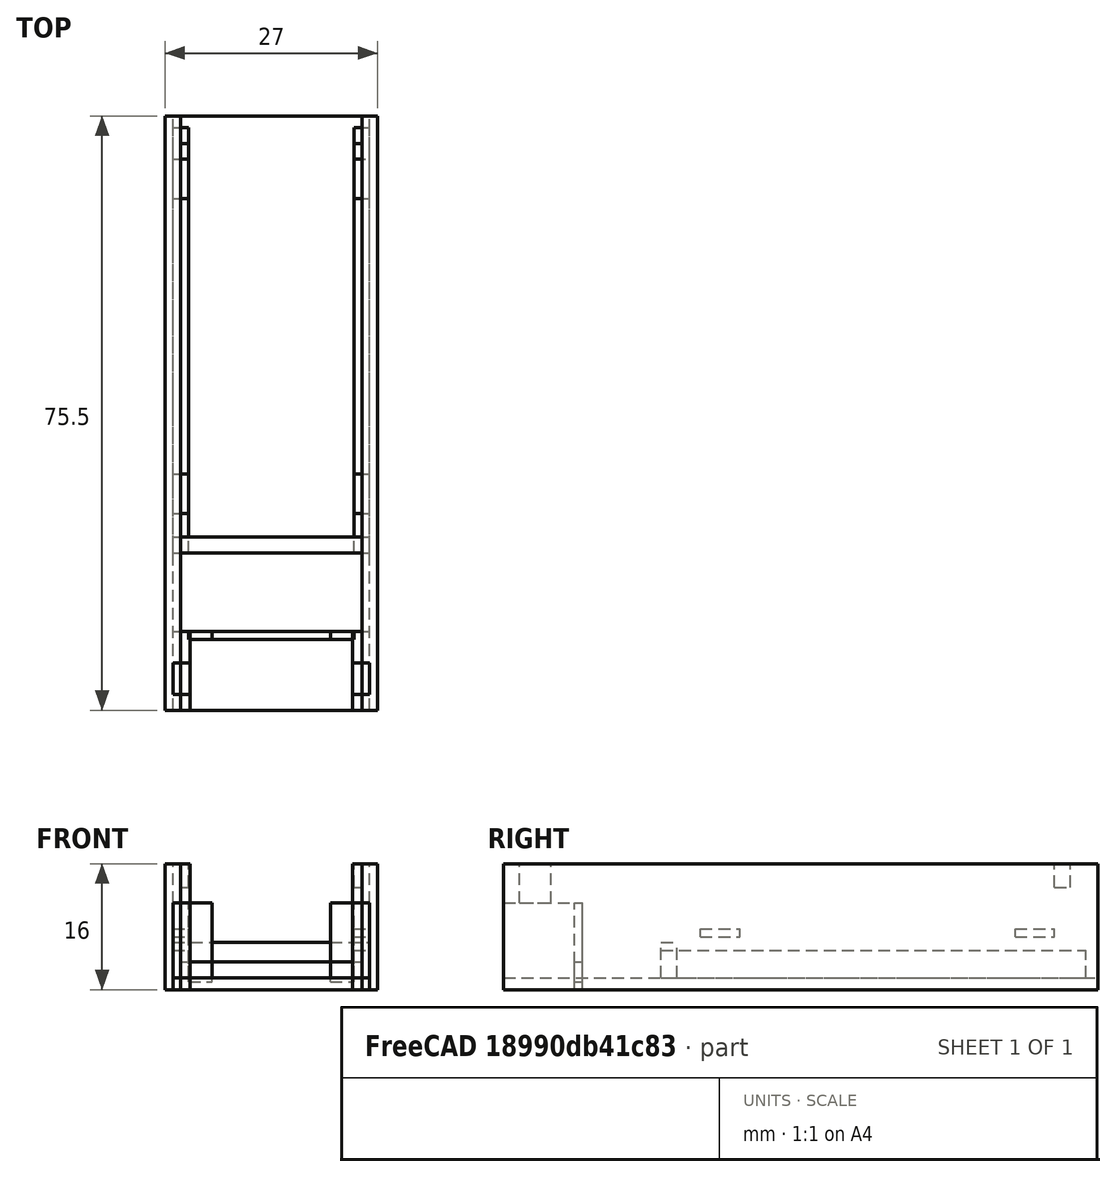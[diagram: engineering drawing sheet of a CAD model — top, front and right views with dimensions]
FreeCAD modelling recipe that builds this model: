
FCSTD DOCUMENT  (FreeCAD 0.20R29177 (Git))
Label: Anlogic FPGA programer
License: All rights reserved
LicenseURL: http://en.wikipedia.org/wiki/All_rights_reserved
objects: Part::Box×19
note: 19 computed .brp shape members not serialized (recipe doc carries the construction recipe); baked Part::Feature solids carry a one-line shape summary decoded from their .brp

FEATURE [Part::Box] Box  label="Kocka"
  AttacherType = Attacher::AttachEngine3D
  Height = 1.5
  Length = 25
  Placement = pos=(0,-20,0) rot=(0,0,1;0rad)
  Width = 75.5
FEATURE [Part::Box] Box001  label="Kocka001"
  AttacherType = Attacher::AttachEngine3D
  Height = 3.5
  Length = 2
  Placement = pos=(0,0,1.5) rot=(0,0,1;0rad)
  Width = 54
FEATURE [Part::Box] Box002  label="Kocka002"
  AttacherType = Attacher::AttachEngine3D
  Height = 16
  Length = 2
  Placement = pos=(-1,-20,0) rot=(0,0,1;0rad)
  Width = 75.5
FEATURE [Part::Box] Box005  label="Kocka005"
  AttacherType = Attacher::AttachEngine3D
  Height = 3.5
  Length = 2
  Placement = pos=(23,0,1.5) rot=(0,0,1;0rad)
  Width = 54
FEATURE [Part::Box] Box006  label="Kocka006"
  AttacherType = Attacher::AttachEngine3D
  Height = 16
  Length = 2
  Placement = pos=(24,-20,0) rot=(0,0,1;0rad)
  Width = 75.5
FEATURE [Part::Box] Box007  label="Kocka007"
  AttacherType = Attacher::AttachEngine3D
  Height = 4.5
  Length = 25
  Placement = pos=(0,0,1.5) rot=(0,0,1;0rad)
  Width = 2
FEATURE [Part::Box] Box008  label="Kocka008"
  AttacherType = Attacher::AttachEngine3D
  Height = 1
  Length = 2
  Placement = pos=(0,5,6.7) rot=(0,0,1;0rad)
  Width = 5
FEATURE [Part::Box] Box009  label="Kocka009"
  AttacherType = Attacher::AttachEngine3D
  Height = 1
  Length = 2
  Placement = pos=(0,45,6.7) rot=(0,0,1;0rad)
  Width = 5
FEATURE [Part::Box] Box012  label="Kocka012"
  AttacherType = Attacher::AttachEngine3D
  Height = 1
  Length = 2
  Placement = pos=(23,5,6.7) rot=(0,0,1;0rad)
  Width = 5
FEATURE [Part::Box] Box014  label="Kocka014"
  AttacherType = Attacher::AttachEngine3D
  Height = 1
  Length = 2
  Placement = pos=(23,45,6.7) rot=(0,0,1;0rad)
  Width = 5
FEATURE [Part::Box] Box015  label="Kocka015"
  AttacherType = Attacher::AttachEngine3D
  Height = 11
  Length = 2.2
  Placement = pos=(0,-20,0) rot=(0,0,1;0rad)
  Width = 10
FEATURE [Part::Box] Box016  label="Kocka016"
  AttacherType = Attacher::AttachEngine3D
  Height = 11
  Length = 2.2
  Placement = pos=(22.8,-20,0) rot=(0,0,1;0rad)
  Width = 10
FEATURE [Part::Box] Box017  label="Kocka017"
  AttacherType = Attacher::AttachEngine3D
  Height = 3.5
  Length = 23
  Placement = pos=(1,-11,0) rot=(0,0,1;0rad)
  Width = 1
FEATURE [Part::Box] Box018  label="Kocka018"
  AttacherType = Attacher::AttachEngine3D
  Height = 5
  Length = 2.2
  Placement = pos=(0,-18,11) rot=(0,0,1;0rad)
  Width = 4
FEATURE [Part::Box] Box019  label="Kocka019"
  AttacherType = Attacher::AttachEngine3D
  Height = 5
  Length = 2.2
  Placement = pos=(22.8,-18,11) rot=(0,0,1;0rad)
  Width = 4
FEATURE [Part::Box] Box020  label="Kocka020"
  AttacherType = Attacher::AttachEngine3D
  Height = 10
  Length = 3
  Placement = pos=(2,-11,1) rot=(0,0,1;0rad)
  Width = 1
FEATURE [Part::Box] Box021  label="Kocka021"
  AttacherType = Attacher::AttachEngine3D
  Height = 10
  Length = 3
  Placement = pos=(20,-11,1) rot=(0,0,1;0rad)
  Width = 1
FEATURE [Part::Box] Box022  label="Kocka022"
  AttacherType = Attacher::AttachEngine3D
  Height = 3
  Length = 1
  Placement = pos=(1,50,13) rot=(0,0,1;0rad)
  Width = 2
FEATURE [Part::Box] Box023  label="Kocka023"
  AttacherType = Attacher::AttachEngine3D
  Height = 3
  Length = 1
  Placement = pos=(23,50,13) rot=(0,0,1;0rad)
  Width = 2
